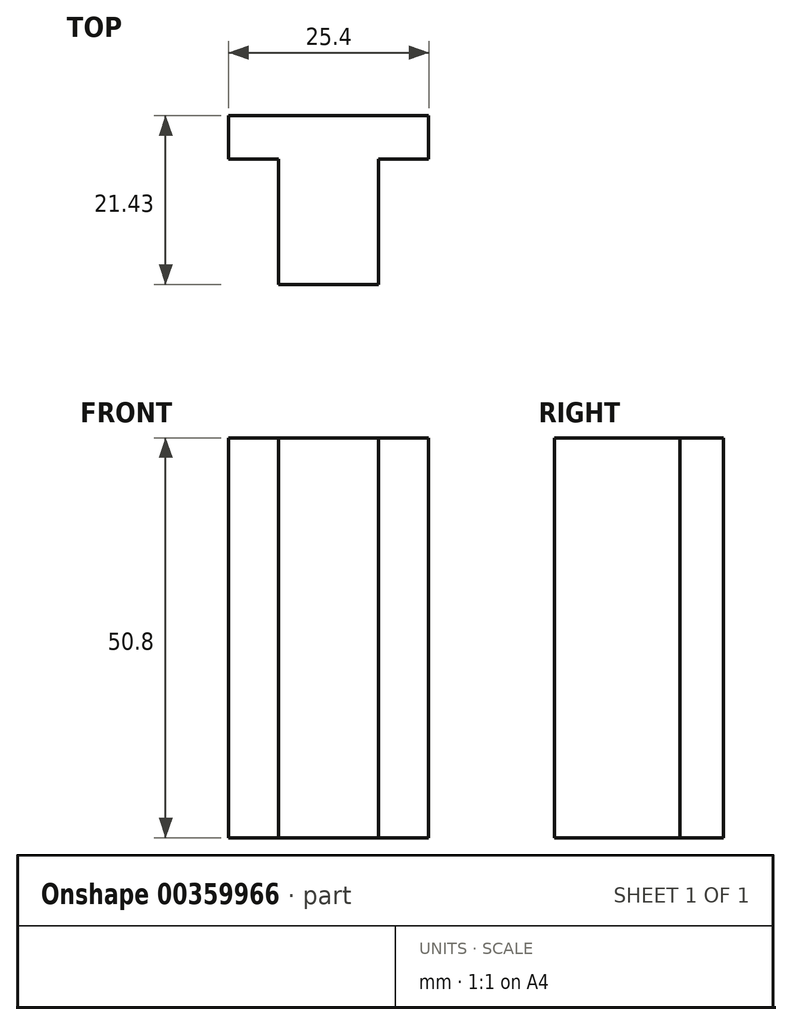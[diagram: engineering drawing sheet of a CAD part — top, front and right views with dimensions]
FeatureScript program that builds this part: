
annotation { "Feature Type Name" : "Feature", "Feature Type Description" : "" }
export const myFeature = defineFeature(function(context is Context, id is Id, definition is map)
    precondition{}
    {
        {
            var Q0;
            Q0=qCreatedBy(makeId("Top.planeOp"),FACE);
            var sketch = newSketch(context, id + "F0", { "sketchPlane" : qUnion([Q0])});
            skLineSegment(sketch, "E0", {"start": v(15.47, 0) * mm, "end": v(15.47, 15.9) * mm});
            skLineSegment(sketch, "E1", {"start": v(15.47, 15.9) * mm, "end": v(9.12, 15.9) * mm});
            skLineSegment(sketch, "E2", {"start": v(9.12, 15.9) * mm, "end": v(9.12, 21.43) * mm});
            skLineSegment(sketch, "E3", {"start": v(9.12, 21.43) * mm, "end": v(34.52, 21.43) * mm});
            skLineSegment(sketch, "E4", {"start": v(34.52, 21.43) * mm, "end": v(34.52, 15.9) * mm});
            skLineSegment(sketch, "E5", {"start": v(34.52, 15.9) * mm, "end": v(28.17, 15.9) * mm});
            skLineSegment(sketch, "E6", {"start": v(28.17, 15.9) * mm, "end": v(28.17, 0) * mm});
            skLineSegment(sketch, "E7", {"start": v(28.17, 0) * mm, "end": v(15.47, 0) * mm});
            skSolve(sketch);
        }
        {
            var Q0;
            Q0 = qSketchRegion(id + "F0", true);
            extrude(context, id + "F1", {"entities" : qUnion([Q0]), "depth" : 50.8 * mm});
        }
    });
